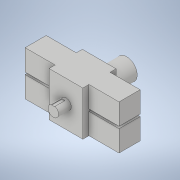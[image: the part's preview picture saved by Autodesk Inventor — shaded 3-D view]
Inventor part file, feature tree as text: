
AUTODESK INVENTOR PART (.ipt)
format: ipt  version: 2021 (Build 250183000, 183)  size: 157,184 bytes
history: native  units: mm
features: extrude x6, sketch x6
ambient origin geometry x8: Origin, YZ Plane, XZ Plane, XY Plane, X Axis, Y Axis, Z Axis, Center Point
bodies: Solid1 (feature_tree)
feature tree (12):
  extrude  "Extrusion1"  Depth=133.35mm
  extrude  "Extrusion2"  Depth=50.8mm
  extrude  "Extrusion3"  Depth=31.75mm
  extrude  "Extrusion4"  Depth=63.5mm
  extrude  "Extrusion5"  Depth=18.288mm
  extrude  "Extrusion6"  Depth=63.499mm
  sketch  "Sketch1"  dims[d1=101.6mm d2=133.35mm]
  sketch  "Sketch2"  dims[d3=66.75mm d4=50.8mm]
  sketch  "Sketch3"  dims[d5=100.075mm d6=0.0mm d7=31.75mm]
  sketch  "Sketch4"  dims[d8=38.1mm d9=0.0mm d10=63.5mm]
  sketch  "Sketch5"  dims[d11=82.55mm d12=0.0mm d13=18.288mm]
  sketch  "Sketch7"  dims[d14=18.288mm d15=63.499mm d16=63.499mm d17=63.499mm d18=90.424mm d19=0.0mm d20=90.424mm d21=0.0mm d22=10.0mm d23=5.0mm d24=30.0mm d25=0.0mm]
